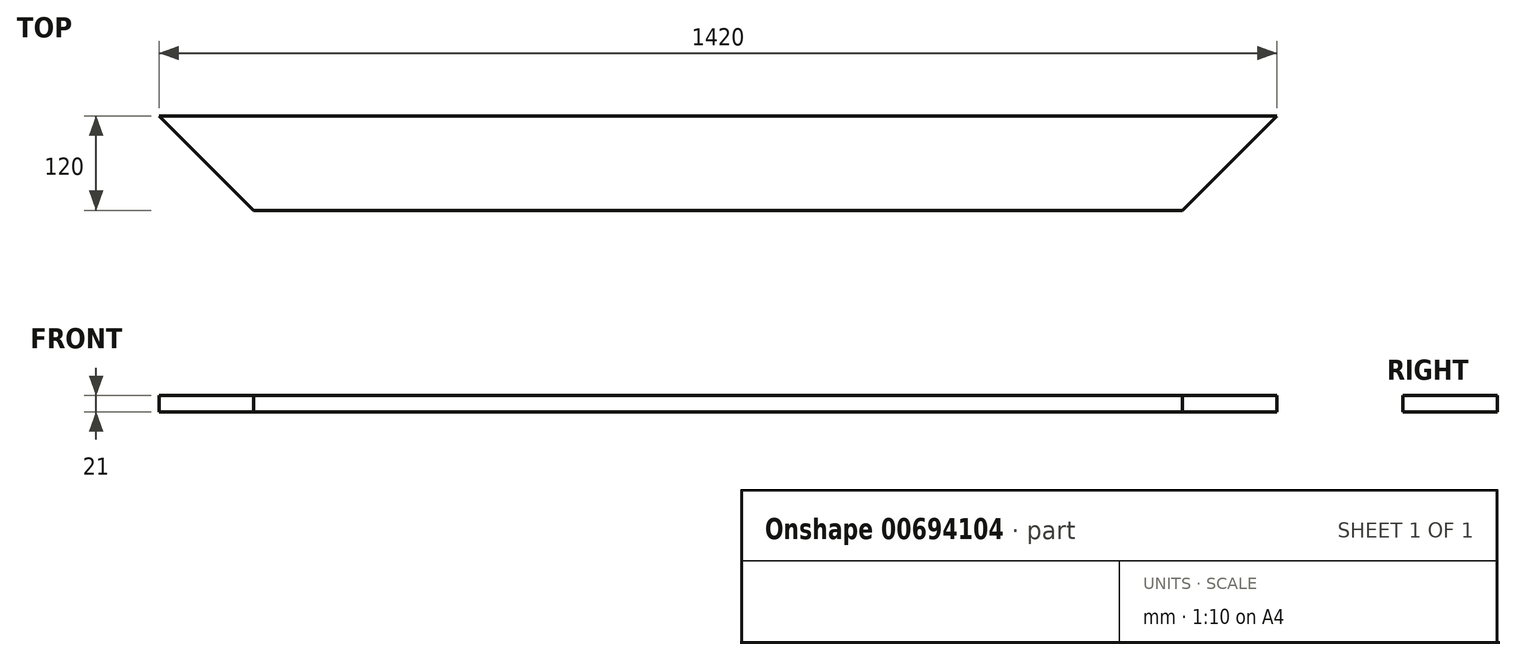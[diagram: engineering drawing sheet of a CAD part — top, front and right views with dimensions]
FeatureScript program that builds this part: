
annotation { "Feature Type Name" : "Feature", "Feature Type Description" : "" }
export const myFeature = defineFeature(function(context is Context, id is Id, definition is map)
    precondition{}
    {
        {
            var Q0;
            Q0=qCreatedBy(makeId("Top.planeOp"),FACE);
            var sketch = newSketch(context, id + "F0", { "sketchPlane" : qUnion([Q0])});
            skLineSegment(sketch, "E0.bottom", {"start": v(-710, 60) * mm, "end": v(710, 60) * mm});
            skLineSegment(sketch, "E0.top", {"start": v(-710, -60) * mm, "end": v(710, -60) * mm});
            skLineSegment(sketch, "E0.left", {"start": v(-710, 60) * mm, "end": v(-710, -60) * mm});
            skLineSegment(sketch, "E0.right", {"start": v(710, 60) * mm, "end": v(710, -60) * mm});
            skSolve(sketch);
        }
        {
            var Q0;
            Q0=makeQuery(id+"F0.imprint","IMPRINT",FACE,{"disambiguationData":[TD([[makeQuery(id+"F0.imprint","IMPRINT",EDGE,{"derivedFrom":sQuery(id+"F0.wireOp",EDGE,"E0.bottom")}),-1.0]])]});
            extrude(context, id + "F1", {"entities" : qUnion([Q0]), "depth" : 21 * mm, "offsetDistance" : 25 * mm});
        }
        {
            var Q0;
            Q0=makeQuery(id+"F1.opExtrude","SWEPT_EDGE",EDGE,{"disambiguationData":[OSD([sQuery(id+"F0.wireOp",EDGE,"E0.top"),sQuery(id+"F0.wireOp",EDGE,"E0.left")])]});
            var Q1;
            Q1=makeQuery(id+"F1.opExtrude","SWEPT_EDGE",EDGE,{"disambiguationData":[OSD([sQuery(id+"F0.wireOp",EDGE,"E0.top"),sQuery(id+"F0.wireOp",EDGE,"E0.right")])]});
            chamfer(context, id + "F2", {"entities" : qUnion([Q0, Q1]), "width" : 120 * mm, "tangentPropagation" : true});
        }
    });
